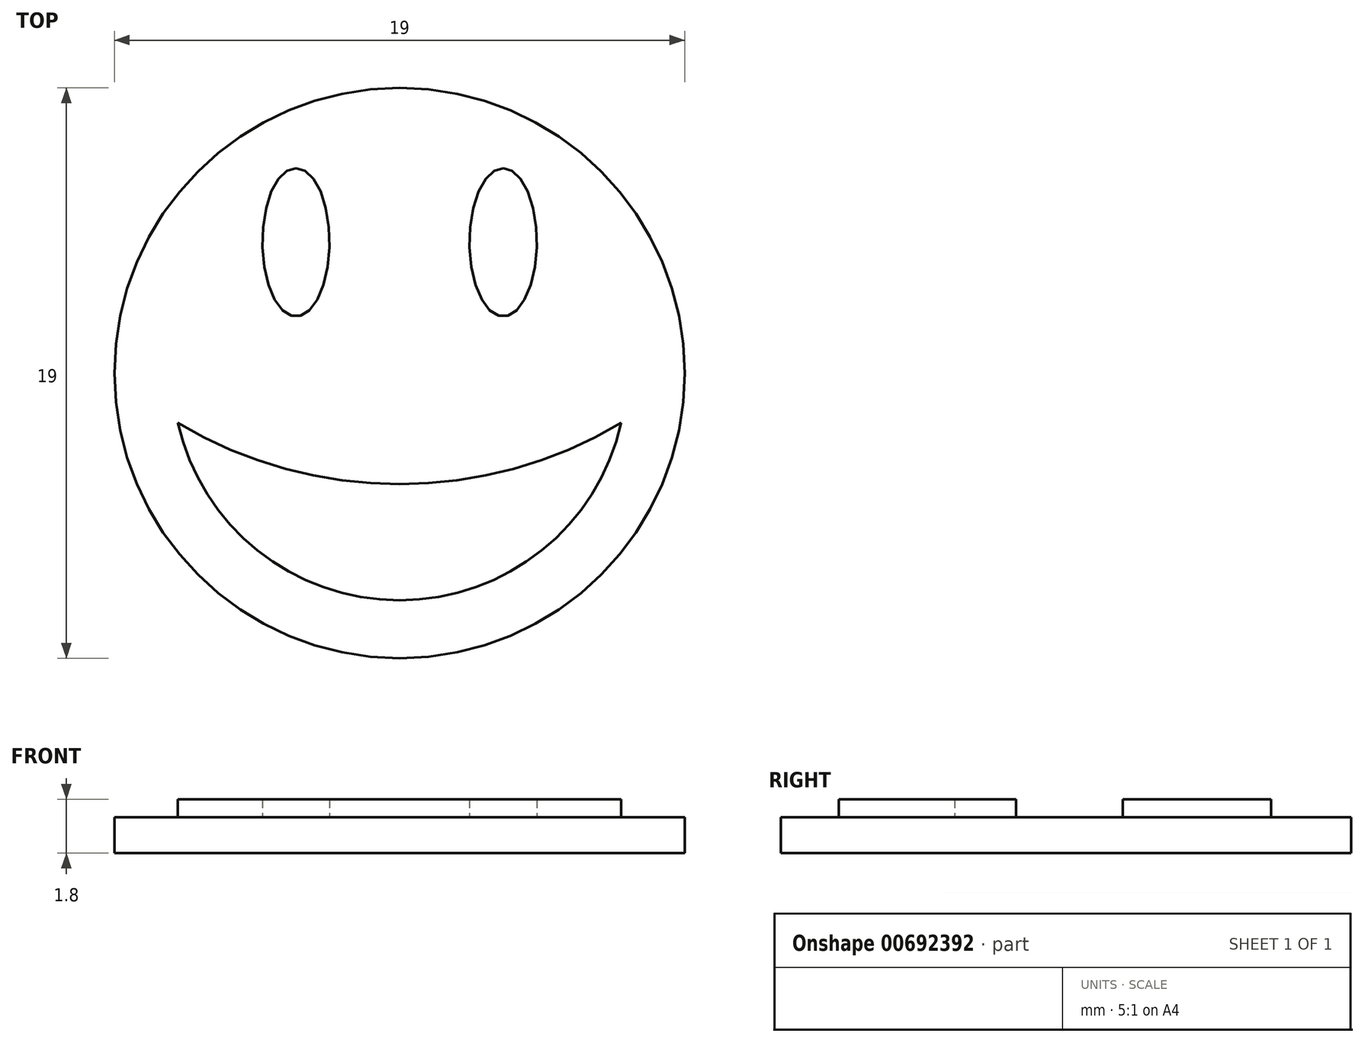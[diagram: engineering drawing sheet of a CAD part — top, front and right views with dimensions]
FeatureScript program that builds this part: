
annotation { "Feature Type Name" : "Feature", "Feature Type Description" : "" }
export const myFeature = defineFeature(function(context is Context, id is Id, definition is map)
    precondition{}
    {
        {
            var Q0;
            Q0=qCreatedBy(makeId("Top.planeOp"),FACE);
            var sketch = newSketch(context, id + "F0", { "sketchPlane" : qUnion([Q0])});
            skCircle(sketch, "E0", {"center": v(0, 0) * mm, "radius": 9.5 * mm});
            skSolve(sketch);
        }
        {
            var Q0;
            Q0=qSketchRegion(id+"F0",true);
            extrude(context, id + "F1", {"entities" : qUnion([Q0]), "depth" : 1.2 * mm, "offsetDistance" : 25 * mm});
        }
        {
            var Q0;
            Q0=makeQuery(id+"F1.opExtrude","CAP_FACE",FACE,{"disambiguationData":[OSD([sQuery(id+"F0.wireOp",EDGE,"E0")])],"isStart":false});
            var sketch = newSketch(context, id + "F2", { "sketchPlane" : qUnion([Q0])});
            skArc(sketch, "E1", {"start": v(0, -7.57) * mm, "mid": v(4.73, -5.91) * mm, "end": v(7.39, -1.66) * mm});
            skArc(sketch, "E2.MirrorCS", {"start": v(0, -7.57) * mm, "mid": v(-4.73, -5.91) * mm, "end": v(-7.39, -1.66) * mm});
            skArc(sketch, "E3", {"start": v(-7.39, -1.66) * mm, "mid": v(0, -3.7) * mm, "end": v(7.39, -1.66) * mm});
            skEllipse(sketch, "E4", {"center": v(-3.45, 4.36) * mm, "majorRadius": 2.47 * mm, "minorRadius": 1.12 * mm, "majorAxis": v(0, 1)});
            skEllipse(sketch, "E5.MirrorC", {"center": v(3.45, 4.36) * mm, "majorRadius": 2.47 * mm, "minorRadius": 1.12 * mm, "majorAxis": v(0, 1)});
            skSolve(sketch);
        }
        {
            var Q0;
            Q0 = qSketchRegion(id + "F2", true);
            extrude(context, id + "F3", {"entities" : qUnion([Q0]), "operationType" : NewBodyOperationType.ADD, "depth" : .6 * mm, "offsetDistance" : 25 * mm});
        }
    });
